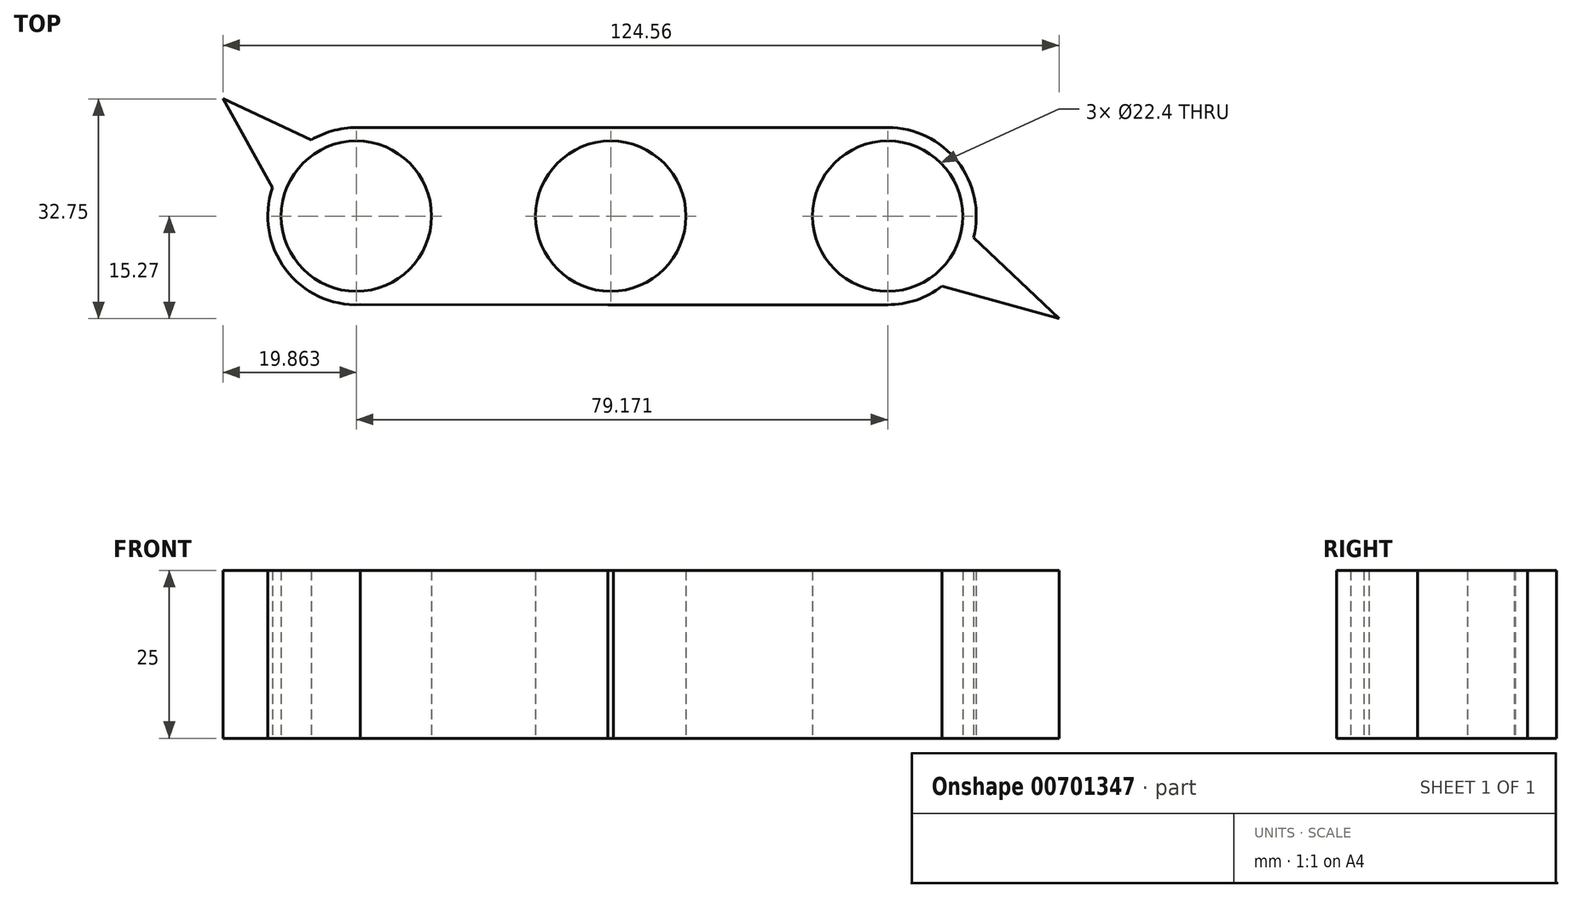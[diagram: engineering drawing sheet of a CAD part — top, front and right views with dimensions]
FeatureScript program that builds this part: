
annotation { "Feature Type Name" : "Feature", "Feature Type Description" : "" }
export const myFeature = defineFeature(function(context is Context, id is Id, definition is map)
    precondition{}
    {
        {
            var Q0;
            Q0=qCreatedBy(makeId("Top.planeOp"),FACE);
            var sketch = newSketch(context, id + "F0", { "sketchPlane" : qUnion([Q0])});
            skCircle(sketch, "E0", {"center": v(0, 0) * mm, "radius": 11.2 * mm});
            skCircle(sketch, "E1", {"center": v(0, 0) * mm, "radius": 13.2 * mm});
            skCircle(sketch, "E2", {"center": v(-37.9, 0) * mm, "radius": 11.2 * mm});
            skArc(sketch, "E3", {"start": v(-37.35, 13.19) * mm, "mid": v(-51.1, 0) * mm, "end": v(-37.34, -13.19) * mm});
            skCircle(sketch, "E4", {"center": v(41.26, 0) * mm, "radius": 11.2 * mm});
            skArc(sketch, "E5", {"start": v(41.26, -13.2) * mm, "mid": v(54.46, 0) * mm, "end": v(41.26, 13.2) * mm});
            skLineSegment(sketch, "E6", {"start": v(-37.35, 13.19) * mm, "end": v(41.26, 13.2) * mm});
            skLineSegment(sketch, "E7", {"start": v(-37.34, -13.19) * mm, "end": v(41.26, -13.2) * mm});
            skLineSegment(sketch, "E8", {"start": v(-50.4, 4.24) * mm, "end": v(-57.77, 17.48) * mm});
            skLineSegment(sketch, "E9", {"start": v(-57.77, 17.48) * mm, "end": v(-44.64, 11.36) * mm});
            skLineSegment(sketch, "E10", {"start": v(49.34, -10.44) * mm, "end": v(66.8, -15.27) * mm});
            skLineSegment(sketch, "E11", {"start": v(54.07, -3.2) * mm, "end": v(66.8, -15.27) * mm});
            skSolve(sketch);
        }
        {
            var Q0;
            Q0 = qSketchRegion(id + "F0", true);
            extrude(context, id + "F1", {"entities" : qUnion([Q0]), "depth" : 25 * mm, "offsetDistance" : 25 * mm});
        }
    });
